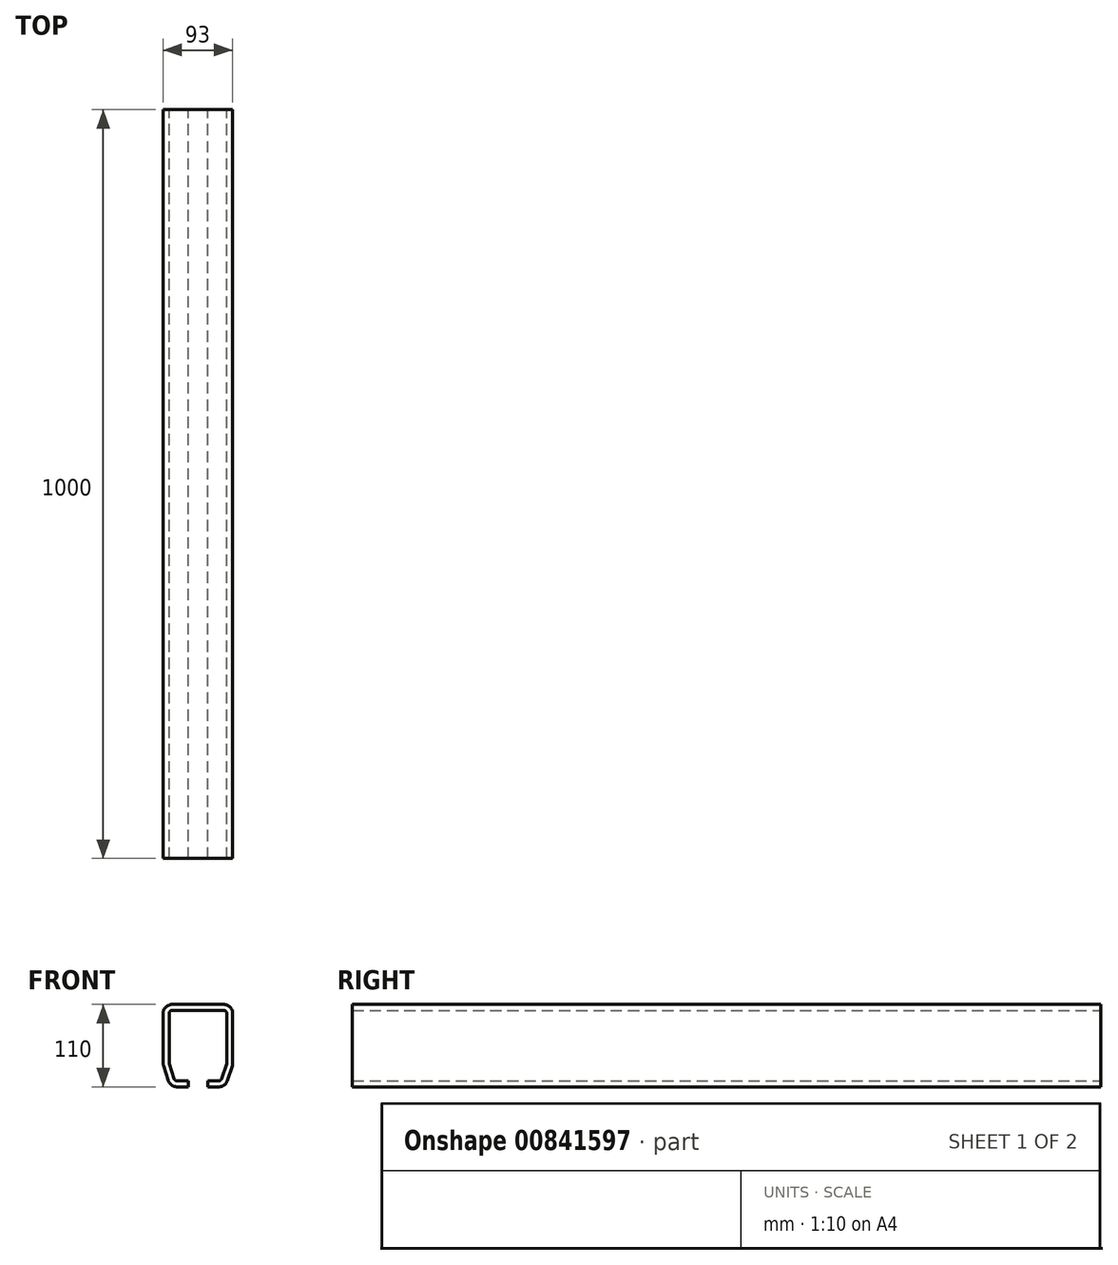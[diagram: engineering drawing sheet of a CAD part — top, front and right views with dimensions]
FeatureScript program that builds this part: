
annotation { "Feature Type Name" : "Feature", "Feature Type Description" : "" }
export const myFeature = defineFeature(function(context is Context, id is Id, definition is map)
    precondition{}
    {
        {
            var Q0;
            Q0=qCreatedBy(makeId("Front.planeOp"),FACE);
            var sketch = newSketch(context, id + "F0", { "sketchPlane" : qUnion([Q0])});
            skLineSegment(sketch, "E0", {"start": v(-39.45, -46.7) * mm, "end": v(-45.91, -26.8) * mm});
            skLineSegment(sketch, "E1", {"start": v(39.45, -46.7) * mm, "end": v(45.91, -26.8) * mm});
            skLineSegment(sketch, "E2", {"start": v(-13, -55) * mm, "end": v(-28.03, -55) * mm});
            skLineSegment(sketch, "E3", {"start": v(13, -55) * mm, "end": v(28.03, -55) * mm});
            skLineSegment(sketch, "E4", {"start": v(-46.5, -23.1) * mm, "end": v(-46.5, 43) * mm});
            skLineSegment(sketch, "E5", {"start": v(-34.5, 55) * mm, "end": v(34.5, 55) * mm});
            skLineSegment(sketch, "E6", {"start": v(46.5, 43) * mm, "end": v(46.5, -23.1) * mm});
            skArc(sketch, "E7", {"start": v(-34.5, 43.47) * mm, "mid": v(-34.83, 43.33) * mm, "end": v(-34.97, 43) * mm});
            skArc(sketch, "E8", {"start": v(34.97, 43) * mm, "mid": v(34.83, 43.33) * mm, "end": v(34.5, 43.47) * mm});
            skArc(sketch, "E9", {"start": v(-34.97, -23.1) * mm, "mid": v(-34.97, -23.17) * mm, "end": v(-34.95, -23.25) * mm});
            skArc(sketch, "E10", {"start": v(34.95, -23.25) * mm, "mid": v(34.97, -23.17) * mm, "end": v(34.97, -23.1) * mm});
            skArc(sketch, "E11", {"start": v(28.03, -43.47) * mm, "mid": v(28.31, -43.38) * mm, "end": v(28.48, -43.15) * mm});
            skArc(sketch, "E12", {"start": v(-28.48, -43.15) * mm, "mid": v(-28.31, -43.38) * mm, "end": v(-28.03, -43.47) * mm});
            skLineSegment(sketch, "E13", {"start": v(13, -47) * mm, "end": v(28.03, -47) * mm});
            skArc(sketch, "E14", {"start": v(28.03, -43.16) * mm, "mid": v(28.13, -43.13) * mm, "end": v(28.18, -43.05) * mm});
            skLineSegment(sketch, "E15", {"start": v(31.84, -44.24) * mm, "end": v(38.3, -24.34) * mm});
            skLineSegment(sketch, "E16", {"start": v(38.5, 43) * mm, "end": v(38.5, -23.1) * mm});
            skArc(sketch, "E17", {"start": v(34.66, 43) * mm, "mid": v(34.61, 43.11) * mm, "end": v(34.5, 43.16) * mm});
            skLineSegment(sketch, "E18", {"start": v(-34.5, 47) * mm, "end": v(34.5, 47) * mm});
            skArc(sketch, "E19", {"start": v(-34.5, 43.16) * mm, "mid": v(-34.61, 43.11) * mm, "end": v(-34.66, 43) * mm});
            skLineSegment(sketch, "E20", {"start": v(-38.5, -23.1) * mm, "end": v(-38.5, 43) * mm});
            skLineSegment(sketch, "E21", {"start": v(-31.84, -44.24) * mm, "end": v(-38.3, -24.34) * mm});
            skArc(sketch, "E22", {"start": v(-34.66, -23.1) * mm, "mid": v(-34.66, -23.12) * mm, "end": v(-34.65, -23.15) * mm});
            skArc(sketch, "E23", {"start": v(34.65, -23.15) * mm, "mid": v(34.66, -23.12) * mm, "end": v(34.66, -23.1) * mm});
            skArc(sketch, "E24", {"start": v(-28.18, -43.05) * mm, "mid": v(-28.13, -43.13) * mm, "end": v(-28.03, -43.16) * mm});
            skLineSegment(sketch, "E25", {"start": v(-13, -47) * mm, "end": v(-28.03, -47) * mm});
            skLineSegment(sketch, "E26", {"start": v(13, -55) * mm, "end": v(13, -47) * mm});
            skLineSegment(sketch, "E27", {"start": v(-13, -55) * mm, "end": v(-13, -47) * mm});
            skArc(sketch, "E28", {"start": v(-38.3, -24.34) * mm, "mid": v(-38.45, -23.73) * mm, "end": v(-38.5, -23.1) * mm});
            skArc(sketch, "E29", {"start": v(-45.91, -26.8) * mm, "mid": v(-46.35, -24.98) * mm, "end": v(-46.5, -23.1) * mm});
            skArc(sketch, "E30", {"start": v(38.3, -24.34) * mm, "mid": v(38.45, -23.73) * mm, "end": v(38.5, -23.1) * mm});
            skArc(sketch, "E31", {"start": v(45.91, -26.8) * mm, "mid": v(46.35, -24.98) * mm, "end": v(46.5, -23.1) * mm});
            skArc(sketch, "E32", {"start": v(28.03, -55) * mm, "mid": v(35.09, -52.7) * mm, "end": v(39.45, -46.7) * mm});
            skArc(sketch, "E33", {"start": v(28.03, -47) * mm, "mid": v(30.39, -46.24) * mm, "end": v(31.84, -44.24) * mm});
            skArc(sketch, "E34", {"start": v(-28.03, -47) * mm, "mid": v(-30.39, -46.24) * mm, "end": v(-31.84, -44.24) * mm});
            skArc(sketch, "E35", {"start": v(-28.03, -55) * mm, "mid": v(-35.09, -52.7) * mm, "end": v(-39.45, -46.7) * mm});
            skArc(sketch, "E36", {"start": v(-38.5, 43) * mm, "mid": v(-37.33, 45.83) * mm, "end": v(-34.5, 47) * mm});
            skArc(sketch, "E37", {"start": v(-46.5, 43) * mm, "mid": v(-42.99, 51.49) * mm, "end": v(-34.5, 55) * mm});
            skArc(sketch, "E38", {"start": v(38.5, 43) * mm, "mid": v(37.33, 45.83) * mm, "end": v(34.5, 47) * mm});
            skArc(sketch, "E39", {"start": v(46.5, 43) * mm, "mid": v(42.99, 51.49) * mm, "end": v(34.5, 55) * mm});
            skSolve(sketch);
        }
        {
            var Q0;
            Q0=makeQuery(id+"F0.imprint","IMPRINT",FACE,{"disambiguationData":[TD([[makeQuery(id+"F0.imprint","IMPRINT",EDGE,{"derivedFrom":sQuery(id+"F0.wireOp",EDGE,"E0")}),-1.0]])]});
            extrude(context, id + "F1", {"entities" : qUnion([Q0]), "depth" : 1000 * mm, "offsetDistance" : 25 * mm});
        }
    });
